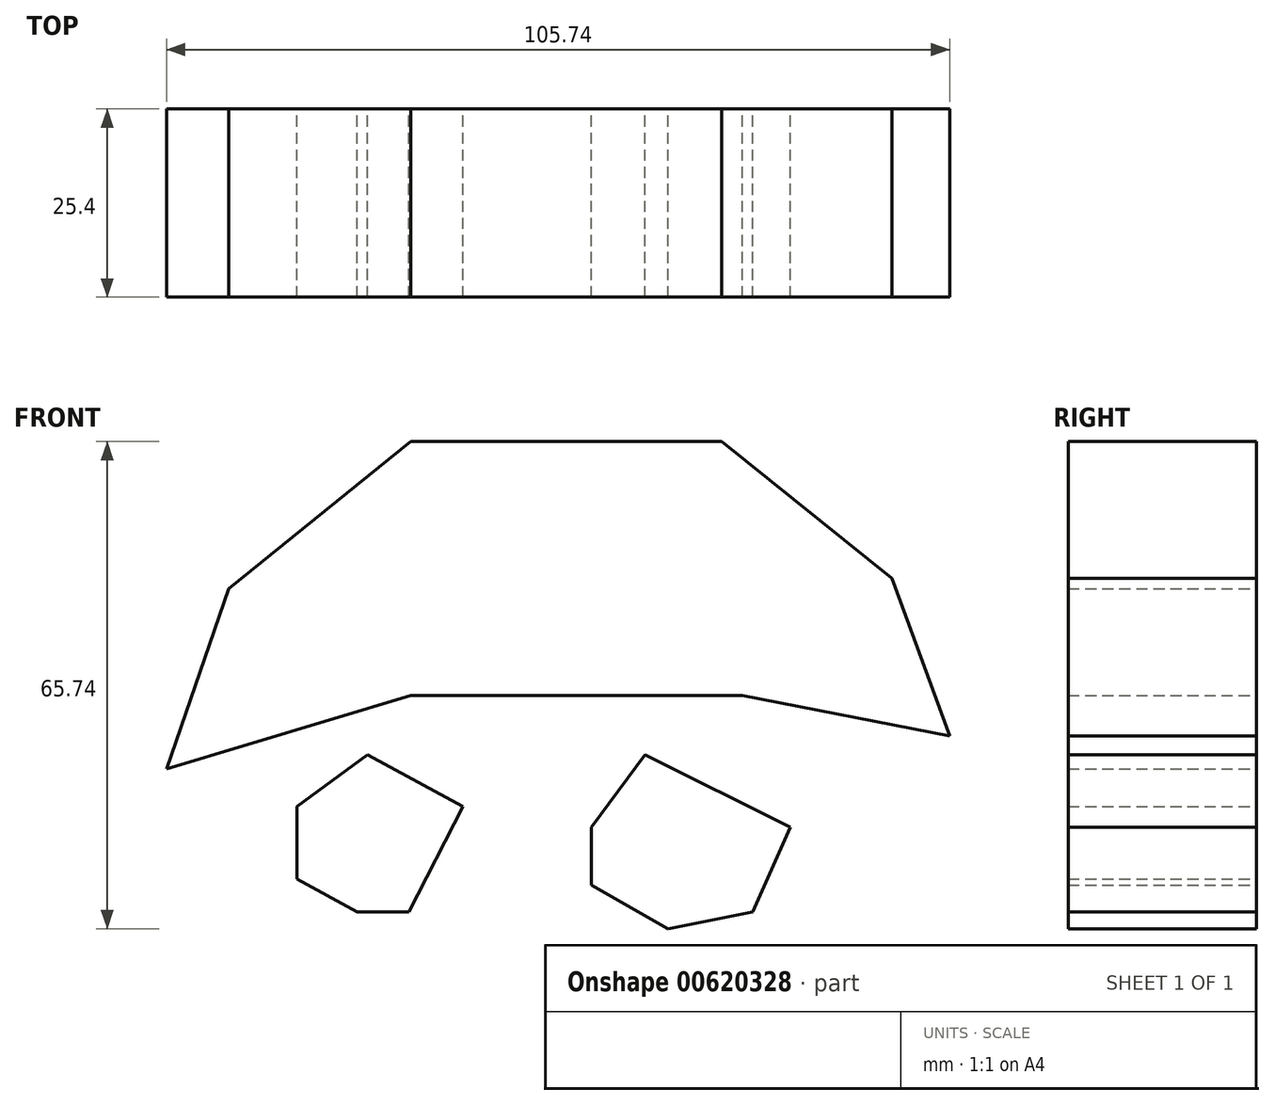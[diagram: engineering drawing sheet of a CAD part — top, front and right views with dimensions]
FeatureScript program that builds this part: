
annotation { "Feature Type Name" : "Feature", "Feature Type Description" : "" }
export const myFeature = defineFeature(function(context is Context, id is Id, definition is map)
    precondition{}
    {
        {
            var Q0;
            Q0=qCreatedBy(makeId("Front.planeOp"),FACE);
            var sketch = newSketch(context, id + "F0", { "sketchPlane" : qUnion([Q0])});
            skLineSegment(sketch, "E0", {"start": v(-43.78, 14.4) * mm, "end": v(-19.16, 34.27) * mm});
            skLineSegment(sketch, "E1", {"start": v(-19.16, 34.27) * mm, "end": v(22.8, 34.27) * mm});
            skLineSegment(sketch, "E2", {"start": v(22.8, 34.27) * mm, "end": v(45.74, 15.8) * mm});
            skLineSegment(sketch, "E3", {"start": v(45.74, 15.8) * mm, "end": v(53.57, -5.46) * mm});
            skLineSegment(sketch, "E4", {"start": v(53.57, -5.46) * mm, "end": v(25.6, 0) * mm});
            skLineSegment(sketch, "E5", {"start": v(25.6, 0) * mm, "end": v(-19.16, 0) * mm});
            skLineSegment(sketch, "E6", {"start": v(-19.16, 0) * mm, "end": v(-52.17, -9.93) * mm});
            skLineSegment(sketch, "E7", {"start": v(-52.17, -9.93) * mm, "end": v(-43.78, 14.4) * mm});
            skSolve(sketch);
        }
        {
            var Q0;
            Q0 = qSketchRegion(id + "F0", true);
            extrude(context, id + "F1", {"entities" : qUnion([Q0]), "depth" : 25.4 * mm, "offsetDistance" : 25.4 * mm});
        }
        {
            var Q0;
            Q0=qCreatedBy(makeId("Front.planeOp"),FACE);
            var sketch = newSketch(context, id + "F2", { "sketchPlane" : qUnion([Q0])});
            skLineSegment(sketch, "E8", {"start": v(-25.04, -7.97) * mm, "end": v(-34.55, -14.97) * mm});
            skLineSegment(sketch, "E9", {"start": v(-34.55, -14.97) * mm, "end": v(-34.55, -24.76) * mm});
            skLineSegment(sketch, "E10", {"start": v(-34.55, -24.76) * mm, "end": v(-26.44, -29.23) * mm});
            skLineSegment(sketch, "E11", {"start": v(-26.44, -29.23) * mm, "end": v(-19.44, -29.23) * mm});
            skLineSegment(sketch, "E12", {"start": v(-19.44, -29.23) * mm, "end": v(-12.17, -14.97) * mm});
            skLineSegment(sketch, "E13", {"start": v(-12.17, -14.97) * mm, "end": v(-25.04, -7.97) * mm});
            skLineSegment(sketch, "E14", {"start": v(12.45, -7.97) * mm, "end": v(5.18, -17.76) * mm});
            skLineSegment(sketch, "E15", {"start": v(5.18, -17.76) * mm, "end": v(5.18, -25.6) * mm});
            skLineSegment(sketch, "E16", {"start": v(5.18, -25.6) * mm, "end": v(15.53, -31.47) * mm});
            skLineSegment(sketch, "E17", {"start": v(15.53, -31.47) * mm, "end": v(27, -29.23) * mm});
            skLineSegment(sketch, "E18", {"start": v(27, -29.23) * mm, "end": v(32.03, -17.76) * mm});
            skLineSegment(sketch, "E19", {"start": v(32.03, -17.76) * mm, "end": v(12.45, -7.97) * mm});
            skSolve(sketch);
        }
        {
            var Q0;
            Q0 = qSketchRegion(id + "F2", true);
            extrude(context, id + "F3", {"entities" : qUnion([Q0]), "depth" : 25.4 * mm, "offsetDistance" : 25.4 * mm});
        }
    });
